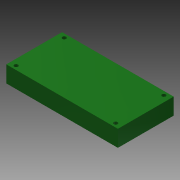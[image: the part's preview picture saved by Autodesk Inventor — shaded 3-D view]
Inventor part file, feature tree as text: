
AUTODESK INVENTOR PART (.ipt)
format: ipt  version: 2013 (Build 170138000, 138)  size: 110,080 bytes
history: native  units: mm
features: sketch x4, extrude x3, hole x1
ambient origin geometry x8: Origin, YZ Plane, XZ Plane, XY Plane, X Axis, Y Axis, Z Axis, Center Point
bodies: Solid1 (feature_tree)
feature tree (8):
  extrude  "Extrusion1"  Depth=101.6mm
  hole  "Hole1"  [1 undecoded]
  extrude  "Extrusion2"  Depth=6.0mm
  extrude  "Extrusion3"  Depth=14.9mm
  sketch  "Sketch1"  dims[d0=50.8mm d2=101.6mm]
  sketch  "Sketch2"  dims[d3=15.0mm d4=0.0mm d5=43.815mm]
  sketch  "Sketch3"  dims[d7=90.678mm]
  sketch  "Sketch4"  dims[d8=3.4mm d9=6.0mm d10=6.5mm d11=3.0mm d12=90.0deg d13=8.0mm d14=20.594885mm d15=6.0mm d16=14.9mm d17=10.0mm d18=10.0mm d19=0.0mm d20=20.0mm d21=15.0mm d22=15.0mm d23=2.0mm d24=10.0mm d25=0.0mm]
note: 1 required parameter value undecoded (feature->parameter linkage not recoverable at this tier; creation-order binding heuristic only, values carry confidence <= 0.55)
